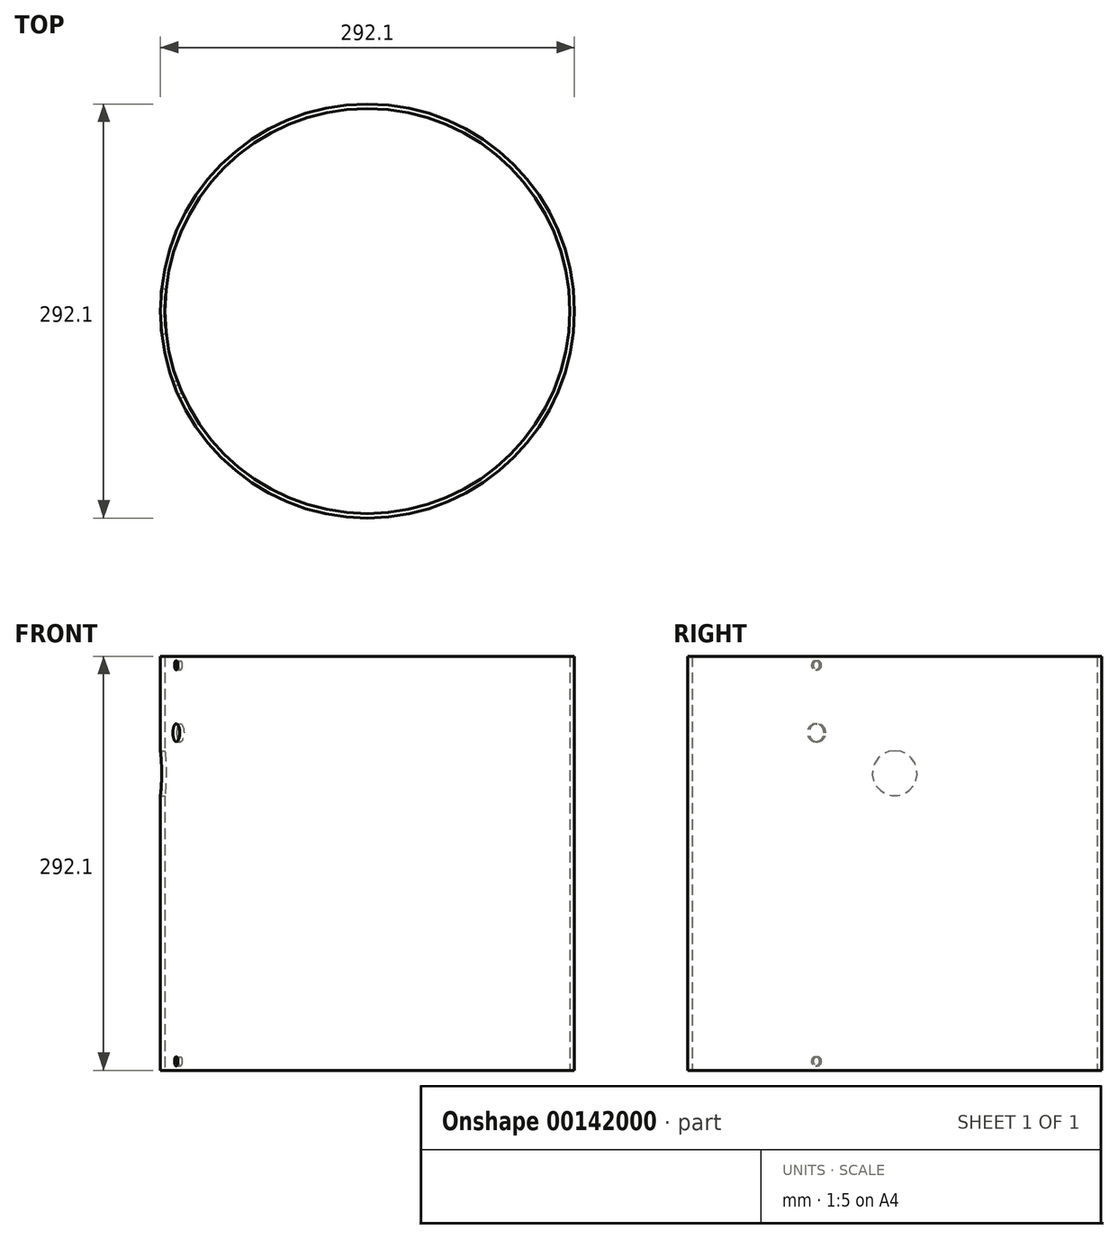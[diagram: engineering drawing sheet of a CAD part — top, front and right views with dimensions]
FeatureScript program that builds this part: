
annotation { "Feature Type Name" : "Feature", "Feature Type Description" : "" }
export const myFeature = defineFeature(function(context is Context, id is Id, definition is map)
    precondition{}
    {
        {
            var Q0;
            Q0=qCreatedBy(makeId("Top.planeOp"),FACE);
            var sketch = newSketch(context, id + "F0", { "sketchPlane" : qUnion([Q0])});
            skCircle(sketch, "E0", {"center": v(0, 0) * mm, "radius": 146.05 * mm});
            skCircle(sketch, "E1", {"center": v(0, 0) * mm, "radius": 142.88 * mm});
            skSolve(sketch);
        }
        {
            var Q0;
            Q0 = qSketchRegion(id + "F0", true);
            extrude(context, id + "F1", {"entities" : qUnion([Q0]), "depth" : 292.1 * mm});
        }
        {
            var Q0;
            Q0=qCreatedBy(makeId("Right.planeOp"),FACE);
            var sketch = newSketch(context, id + "F2", { "sketchPlane" : qUnion([Q0])});
            skCircle(sketch, "E2", {"center": v(0, 209.55) * mm, "radius": 15.88 * mm});
            skLineSegment(sketch, "E3", {"start": v(0, 0) * mm, "end": v(0, 209.55) * mm, "construction": true});
            skSolve(sketch);
        }
        {
            var Q0;
            Q0 = qSketchRegion(id + "F2", true);
            extrude(context, id + "F3", {"entities" : qUnion([Q0]), "operationType" : NewBodyOperationType.REMOVE, "endBound" : BoundingType.THROUGH_ALL, "oppositeDirection" : true, "depth" : 327.03 * mm});
        }
        {
            var Q0;
            Q0=sQuery(id+"F2.wireOp",EDGE,"E3");
            cPlane(context, id + "F4", {"entities" : qUnion([Q0]), "cplaneType" : CPlaneType.LINE_ANGLE, "offset" : 25.4 * mm, "angle" : 22.5 * degree, "width" : 152.4 * mm, "height" : 152.4 * mm});
        }
        {
            var Q0;
            Q0=qCreatedBy(id+"F4.planeOp",FACE);
            var sketch = newSketch(context, id + "F5", { "sketchPlane" : qUnion([Q0])});
            skPoint(sketch, "E4.0", {"position": v(0, 209.55) * mm});
            skCircle(sketch, "E5", {"center": v(0, 238.13) * mm, "radius": 6.35 * mm});
            skSolve(sketch);
        }
        {
            var Q0;
            Q0 = qSketchRegion(id + "F5", true);
            extrude(context, id + "F6", {"entities" : qUnion([Q0]), "operationType" : NewBodyOperationType.REMOVE, "endBound" : BoundingType.THROUGH_ALL, "oppositeDirection" : true, "depth" : 25.4 * mm});
        }
        {
            var Q0;
            Q0=qCreatedBy(id+"F4.planeOp",FACE);
            var sketch = newSketch(context, id + "F7", { "sketchPlane" : qUnion([Q0])});
            skLineSegment(sketch, "E6.0", {"start": v(-142.88, 292.1) * mm, "end": v(142.88, 292.1) * mm, "construction": true});
            skLineSegment(sketch, "E7.0", {"start": v(-146.05, 0) * mm, "end": v(146.05, 0) * mm, "construction": true});
            skCircle(sketch, "E8", {"center": v(0, 285.75) * mm, "radius": 3.18 * mm});
            skCircle(sketch, "E9", {"center": v(0, 6.35) * mm, "radius": 3.18 * mm});
            skSolve(sketch);
        }
        {
            var Q0;
            Q0 = qSketchRegion(id + "F7", true);
            extrude(context, id + "F8", {"entities" : qUnion([Q0]), "operationType" : NewBodyOperationType.REMOVE, "endBound" : BoundingType.THROUGH_ALL, "oppositeDirection" : true, "depth" : 25.4 * mm});
        }
    });
